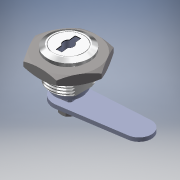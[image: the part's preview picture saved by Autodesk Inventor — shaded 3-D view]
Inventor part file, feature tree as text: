
AUTODESK INVENTOR PART (.ipt)
format: ipt  version: 2016 (Build 200138000, 138)  size: 987,648 bytes
history: native  units: in
note: dims shown in document units (in); Inventor stores cm internally (conversion verified against a paired STEP export)
features: other x7, fillet x3, extrude x2, sketch x2, chamfer x1
ambient origin geometry x8: Origin, YZ Plane, XZ Plane, XY Plane, X Axis, Y Axis, Z Axis, Center Point
bodies: Solid1 (feature_tree), Solid2 (feature_tree), Solid3 (feature_tree), Solid4 (feature_tree), Solid5 (feature_tree), Solid6 (feature_tree), Solid7 (feature_tree)
feature tree (15):
  extrude  "Extrusion1"  Depth=0.0906in
  chamfer  "Chamfer1"  Distance=0.1378in
  extrude  "Extrusion2"  Depth=0.0079in
  fillet  "Fillet1"  Radius=0.0079in
  fillet  "Fillet2"  [1 undecoded]
  fillet  "Fillet3"  [1 undecoded]
  sketch  "Sketch1"  dims[d0=0.1378in d1=0.0in d2=0.0906in d3=0.0787in d4=0.1718in d5=0.1378in d6=0.0in]
  sketch  "Sketch2"  dims[d7=0.0118in d8=0.0079in d9=0.0079in]
  other  "Kunci_1:1"
  other  "insider_2:1"
  other  "leaf_3:1"
  other  "key beneran_4:1"
  other  "ring_5:1"
  other  "hex bolt sp m5_6:1"
  other  "nut m20_7:1"
note: 2 required parameter values undecoded (feature->parameter linkage not recoverable at this tier; creation-order binding heuristic only, values carry confidence <= 0.55)
